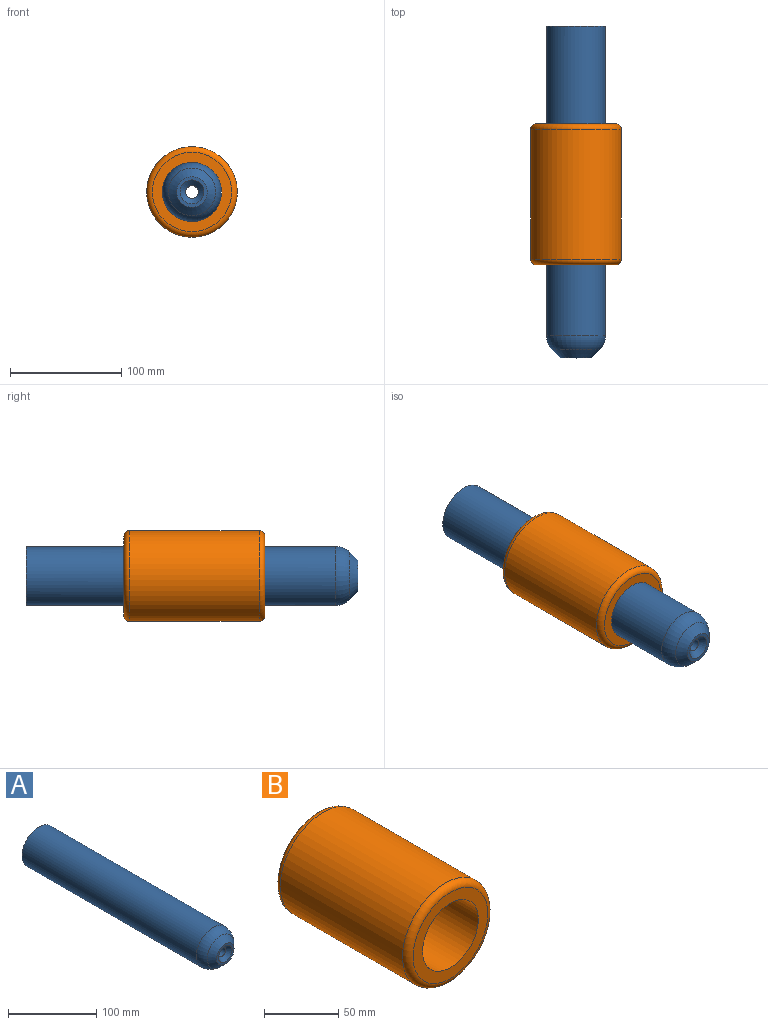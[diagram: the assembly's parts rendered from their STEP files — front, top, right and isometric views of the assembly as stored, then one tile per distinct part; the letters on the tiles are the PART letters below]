
ASSEMBLY  parts=2 mates=1
PART A: 7 faces, bbox 53x298.7x53 mm
  f0: cylinder r=26.52mm len=278.64mm, axis (0,1,0), area 46437.1mm2, adj f2,f6
  f1: plane 27.65x27.65mm, normal (0,-1,0), area 234.3mm2, adj f3,f5
  f2: plane 53.05x53.05mm, normal (0,1,0), area 2107.6mm2, adj f0,f4
  f3: cone r=13.82mm half-angle=45deg, axis (0,1,0), area 1169.8mm2, adj f1,f6
  f4: cylinder r=5.71mm len=293.62mm, axis (0,-1,0), area 10543.6mm2, adj f2,f5
  f5: cone r=5.71mm half-angle=45deg, axis (0,-1,0), area 372.6mm2, adj f1,f4
  f6: torus R=8.74mm, axis (0,-1,0), area 2171.7mm2, adj f0,f3
PART B: 6 faces, bbox 88.2x127x88.2 mm
  f0: cylinder r=26.61mm len=127mm, axis (0,-1,0), area 21231.3mm2, adj f2,f3
  f1: cylinder r=40.75mm len=116.84mm, axis (0,-1,0), area 29917.5mm2, adj f4,f5
  f2: plane 71.35x71.35mm, normal (0,1,0), area 1773.7mm2, adj f0,f5
  f3: plane 71.35x71.35mm, normal (0,-1,0), area 1773.7mm2, adj f0,f4
  f4: torus R=35.67mm, axis (0,-1,0), area 1950.7mm2, adj f1,f3
  f5: torus R=35.67mm, axis (0,-1,0), area 1950.7mm2, adj f1,f2
PLACE A t=(-32.68,-78.36,-17.31)mm
PLACE B t=(-32.68,-73.09,-17.31)mm
MATE slider B.f0 <-> A.f0  axis (0,-1,0) through (-32.68,48.83,-17.31)mm
